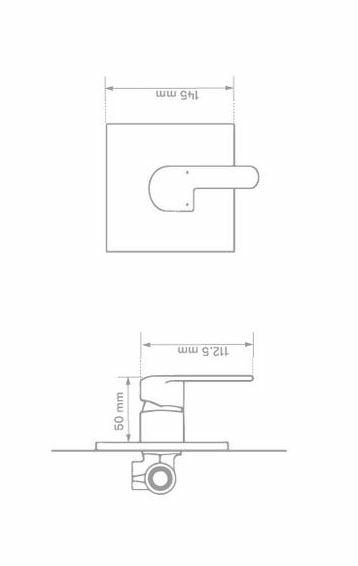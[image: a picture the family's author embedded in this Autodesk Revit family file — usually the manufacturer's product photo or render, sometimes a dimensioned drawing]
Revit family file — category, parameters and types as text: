
# Revit family: 01-1502-11-MEZCLADOR LAVAMANOS PIANA
name_source: partatom
category: Plumbing Fixtures
revit_build: Autodesk Revit 2018 (Build: 20170223_1515(x64)
units: mm (PartAtom-declared; Revit-internal decimal feet)

## family parameters
Cut with Voids When Loaded = No
Host = Face
OmniClass Number = 23.31.11.00
Part Type = Normal
Room Calculation Point = No
Round Connector Dimension = Use Diameter
Shared = No

## types (1)
- 01-1502-11
    Alto = 72 mm  [stored 0.23622 ft]
    Ancho = 207 mm  [stored 0.679134 ft]
    CW Connection = Yes
    Default Elevation = 0 mm  [stored 0 ft]
    Description = Griferia bimando baño
    HW Connection = Yes
    Largo = 88 mm  [stored 0.288714 ft]
    Link Ficha Tecnica = http://infotecnica.gricol.com
    Manufacturer = Gricol
    Model = 01-1502-11
    Plastico ABS + Colorante Gris = Plastico ABS + Colorante Gris
    Plastico ABS Cromado = Plastico ABS Cromado
    Product Name = MEZCLADOR LAVAMANOS PIANA
    Type Image = <None>
    URL = https://www.gricol.com
    Vent Connection = No
    Waste Connection = No

note: [stored X ft] marks values corroborated as IEEE doubles in the binary element streams (Revit-internal decimal feet)

## geometry (parser evidence)
native form markers: Blend x2, Sweep x10
no freeform markers — native parametric forms only
